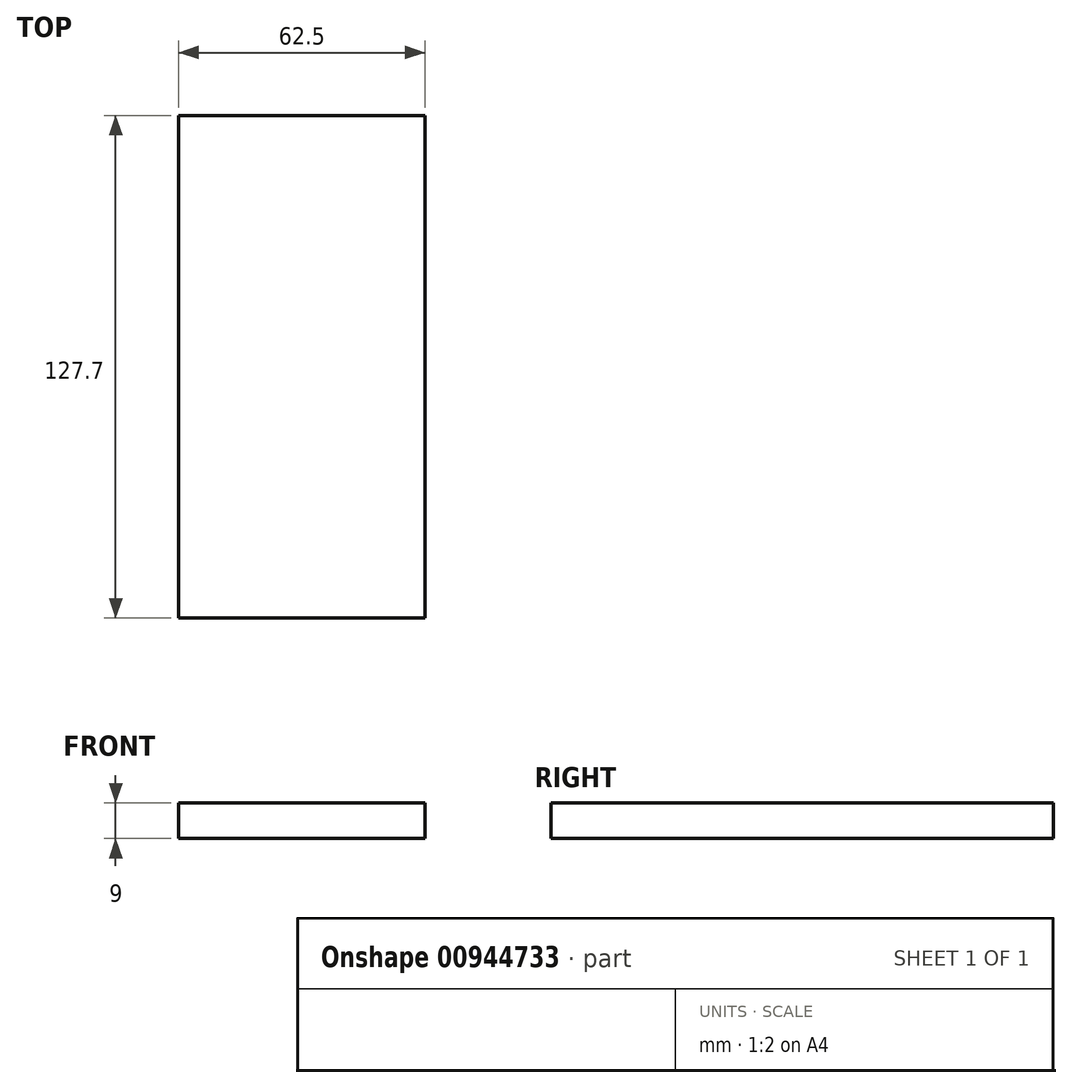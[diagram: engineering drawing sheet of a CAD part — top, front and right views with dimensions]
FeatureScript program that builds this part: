
annotation { "Feature Type Name" : "Feature", "Feature Type Description" : "" }
export const myFeature = defineFeature(function(context is Context, id is Id, definition is map)
    precondition{}
    {
        {
            var Q0;
            Q0=qCreatedBy(makeId("Top.planeOp"),FACE);
            var sketch = newSketch(context, id + "F0", { "sketchPlane" : qUnion([Q0])});
            skLineSegment(sketch, "E0.bottom", {"start": v(0, 0) * mm, "end": v(62.5, 0) * mm});
            skLineSegment(sketch, "E0.top", {"start": v(0, 127.7) * mm, "end": v(62.5, 127.7) * mm});
            skLineSegment(sketch, "E0.left", {"start": v(0, 0) * mm, "end": v(0, 127.7) * mm});
            skLineSegment(sketch, "E0.right", {"start": v(62.5, 0) * mm, "end": v(62.5, 127.7) * mm});
            skLineSegment(sketch, "E1.bottom", {"start": v(2, 2) * mm, "end": v(60.5, 2) * mm});
            skLineSegment(sketch, "E1.top", {"start": v(2, 125.7) * mm, "end": v(60.5, 125.7) * mm});
            skLineSegment(sketch, "E1.left", {"start": v(2, 2) * mm, "end": v(2, 125.7) * mm});
            skLineSegment(sketch, "E1.right", {"start": v(60.5, 2) * mm, "end": v(60.5, 125.7) * mm});
            skSolve(sketch);
        }
        {
            var Q0;
            Q0=makeQuery(id+"F0.imprint","IMPRINT",FACE,{"disambiguationData":[TD([[makeQuery(id+"F0.imprint","IMPRINT",EDGE,{"derivedFrom":sQuery(id+"F0.wireOp",EDGE,"E1.bottom")}),1.0]])]});
            var Q1;
            Q1=makeQuery(id+"F0.imprint","IMPRINT",FACE,{"disambiguationData":[TD([[makeQuery(id+"F0.imprint","IMPRINT",EDGE,{"derivedFrom":sQuery(id+"F0.wireOp",EDGE,"E0.bottom")}),1.0]])]});
            extrude(context, id + "F1", {"entities" : qUnion([Q0, Q1]), "depth" : 9 * mm, "offsetDistance" : 25 * mm});
        }
    });
